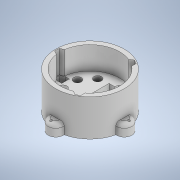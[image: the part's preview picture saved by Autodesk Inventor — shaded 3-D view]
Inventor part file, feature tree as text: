
AUTODESK INVENTOR PART (.ipt)
format: ipt  version: 2021 (Build 250183000, 183)  size: 584,192 bytes
history: native  units: mm
features: extrude x19, sketch x19, fillet x2
ambient origin geometry x8: Origin, YZ Plane, XZ Plane, XY Plane, X Axis, Y Axis, Z Axis, Center Point
bodies: Body1 (feature_tree)
feature tree (40):
  extrude  "Extrusión2"  Depth=30.0mm TaperAngle=0.0deg
  extrude  "Extrusión3"  Depth=10.0mm
  extrude  "Extrusión4"  Depth=40.0mm
  extrude  "Extrusión5"  Depth=10.0mm TaperAngle=0.0deg
  extrude  "Extrusión6"  Depth=30.0mm TaperAngle=360.0deg
  extrude  "Extrusión7"  Depth=5.0mm
  extrude  "Extrusión8"  Depth=10.0mm
  extrude  "Extrusión9"  Depth=10.0mm TaperAngle=0.0deg
  extrude  "Extrusión10"  Depth=10.0mm TaperAngle=360.0deg
  extrude  "Extrusión11"  Depth=42.0mm
  extrude  "Extrusión12"  Depth=10.0mm
  fillet  "Empalme1"  Radius=10.0mm
  extrude  "Extrusión13"  Depth=8.0mm TaperAngle=0.0deg
  extrude  "Extrusión14"  Depth=5.0mm
  fillet  "Empalme2"  Radius=5.0mm
  extrude  "Extrusión15"  Depth=5.0mm
  extrude  "Extrusión16"  Depth=5.0mm TaperAngle=0.0deg
  extrude  "Extrusión17"  Depth=3.0mm
  extrude  "Extrusión18"  Depth=3.0mm
  extrude  "Extrusión19"  Depth=3.0mm TaperAngle=0.0deg
  extrude  "Extrusión20"  Depth=5.0mm TaperAngle=0.0deg
  sketch  "Boceto3"  dims[d7=90.0mm d8=30.0mm d9=0.0mm]
  sketch  "Boceto4"  dims[d10=10.0mm d11=0.0mm d12=20.0mm]
  sketch  "Boceto5"  dims[d13=20.0mm d14=40.0mm]
  sketch  "Boceto6"  dims[d15=20.0mm d16=10.0mm d17=0.0mm]
  sketch  "Boceto7"  dims[d19=10.0mm d20=30.0mm d22=360.0deg]
  sketch  "Boceto10"  dims[d24=10.0mm d25=0.0mm d29=5.0mm]
  sketch  "Boceto13"  dims[d30=90.0mm d32=360.0deg d34=10.0mm]
  sketch  "Boceto14"  dims[d35=10.0mm d38=10.0mm d39=0.0mm]
  sketch  "Boceto15"  dims[d49=10.0mm d51=20.0mm d53=360.0deg]
  sketch  "Boceto17"  dims[d55=12.0mm d56=0.0mm d65=42.0mm]
  sketch  "Boceto19"  dims[d68=42.0mm d70=10.0mm d72=10.0mm]
  sketch  "Boceto22"  dims[d79=8.0mm d80=0.0mm d81=8.0mm d82=0.0mm]
  sketch  "Boceto23"  dims[d86=20.0mm d87=20.0mm d91=5.0mm]
  sketch  "Boceto24"  dims[d92=5.0mm d93=5.0mm]
  sketch  "Boceto25"  dims[d94=5.0mm d95=20.0mm d96=0.0mm]
  sketch  "Boceto27"  dims[d105=100.0mm d106=0.0mm d114=3.0mm]
  sketch  "Boceto28"  dims[d115=3.0mm d116=3.0mm]
  sketch  "Boceto30"  dims[d118=3.0mm d119=100.0mm d120=0.0mm]
  sketch  "Boceto31"  dims[d121=2.0mm d122=28.0mm d123=0.0mm d131=40.0mm d133=360.0deg d135=15.0mm d136=0.0mm d137=5.0mm d147=30.0mm d149=360.0deg d152=30.0mm d153=0.0mm d154=30.0mm d155=0.0mm d169=20.0mm d170=0.0mm d171=5.0mm d172=5.0mm d173=5.0mm d174=20.0mm d175=0.0mm d176=20.0mm d177=0.0mm d178=20.0mm d179=0.0mm d36=0.5mm d37=0.872665mm d165=0.5mm d166=0.872665mm d167=0.5mm d168=0.872665mm]
